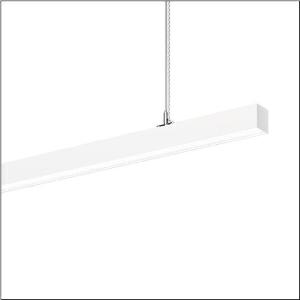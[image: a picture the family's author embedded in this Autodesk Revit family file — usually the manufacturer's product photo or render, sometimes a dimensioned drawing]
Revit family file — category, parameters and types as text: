
# Revit family: silica_r__21_51mx30dc49wb_27b8
name_source: partatom
category: Lighting Fixtures
units: mm (PartAtom-declared; Revit-internal decimal feet)

## family parameters
Cut with Voids When Loaded = No
Host = Face
Light Source = No
Part Type = Normal
Room Calculation Point = No
Round Connector Dimension = Use Diameter
Shared = No

## types (1)
- --- (1 x LED, 10520 lm, 64.1 W, 4000K)
    Apparent Load = 64 VA
    CIE Flux Codes = 47 79 96 57 100
    Color Rendering = 80
    Color Temperature = 4000K
    Default Elevation = 1800 mm
    Description = Silica® 21, office luminaire, primary optical cover: cover, of PMMA, opal, light emission: direct/indirect distribution, primary light characteristic: symmetric, installation type: suspended mounting, LED, rated luminous flux: 10.520lm, luminous efficacy: 164lm/W, light colour: 840, colour temperature: 4000K, with terminal, 3+2-pole, max. 2.5mm², mains connection: 220..240V, AC, 50/60Hz, rated input power: 64.1W, luminaire housing, of aluminium, traffic white (RAL 9016), length: 3.004mm, width: 53mm, height: 53mm, protection rating (complete): IP20, insulation class (complete): insulation class I (protective earthing), certification: CE, permissible operating ambient temperature: 0..+35°C, standard: EN 50419, packaging unit: 1 piece
    Height = 53 mm
    Lamp = 1 x LED
    Lamp Light Flux = 10520 lm
    Lamp Power = 64.1 W
    Lamp count = 1
    Length = 3004 mm
    Luminous efficacy = 164 lm/W
    Manufacturer = Siteco
    ModVariant = No
    Model = 51MX30DC49WB
    Mounting Place = Ceiling
    Mounting Type = Pendant
    Number of Poles = 1
    OnlyDefault = Yes
    Power Factor = 1
    Product Name = Silica® 21
    Product group = office luminaire | ceiling pendant
    ProductGroupID = 902
    Protection Class = Protection class I
    Protection Degree = IP 20
    RLX_Detail_Level = 1
    RLX_Emergency_Light_Flux = 0 lm
    RLX_Emergency_Type = 0
    RLX_Emergency_Type_DB = No
    RlxData = <blob elided: 21321 chars, md5=f97a2657>
    Socket = socket
    Standby Power = 0 W
    System Light Flux = 10520 lm
    System Power = 64 W
    Type Comments = factory setting: luminous flux: 100 % | dim-lin: 254 | 218 mA
    Type Image = l_1297784.jpg
    URL = http://relux.com
    VarID = @adj_047471
    Voltage = 0 V
    Weight = 0.00 kg
    Width = 53 mm

## geometry (parser evidence)
native form markers: Blend x4, Sweep x12
no freeform markers — native parametric forms only
